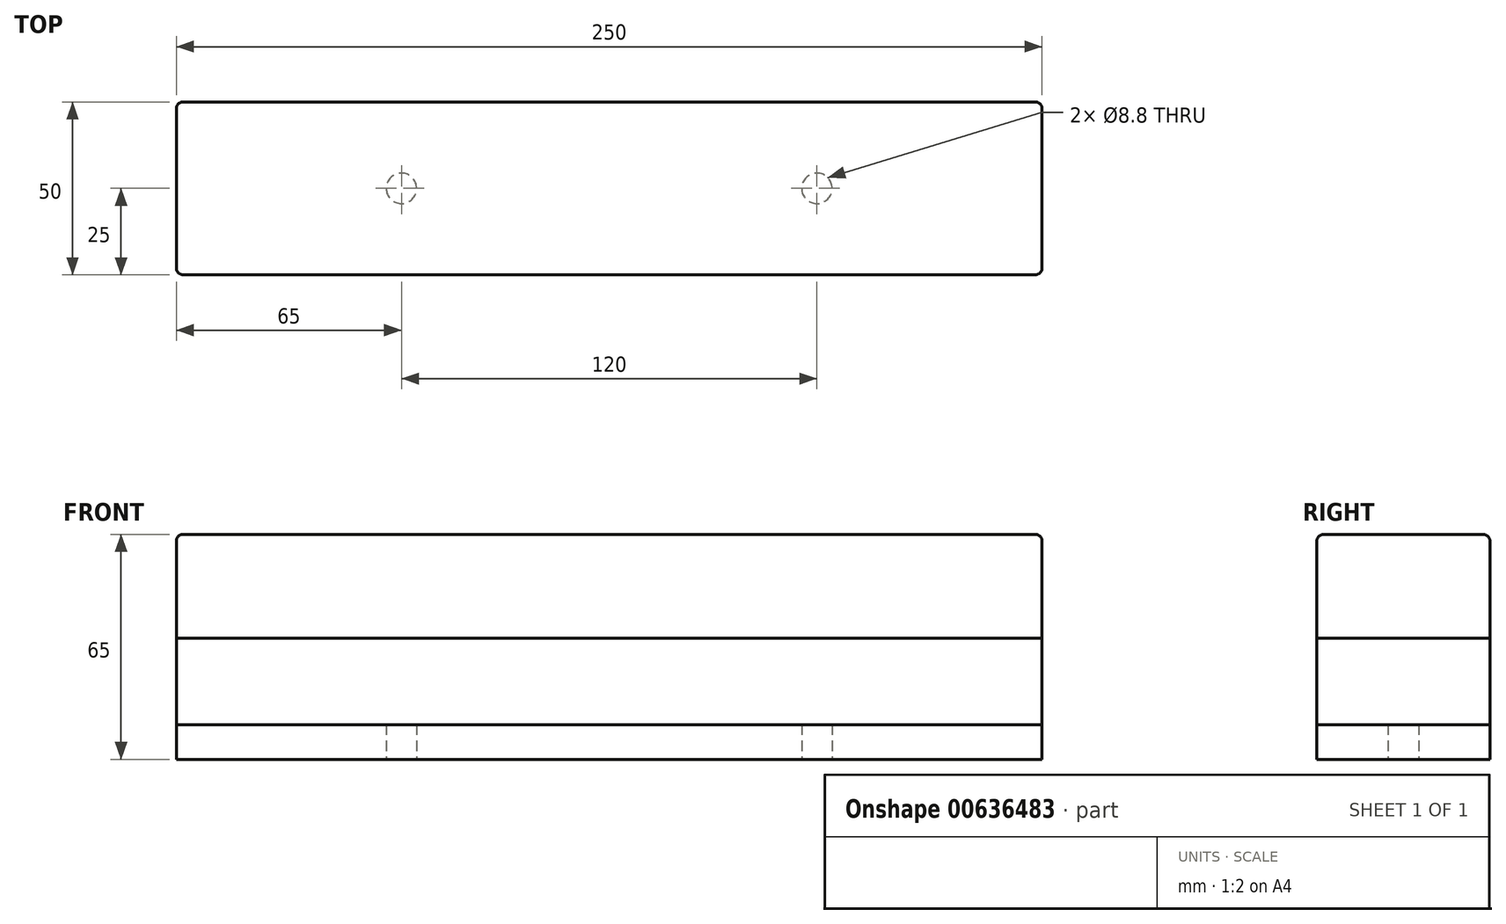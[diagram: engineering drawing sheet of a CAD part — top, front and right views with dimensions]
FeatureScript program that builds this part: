
annotation { "Feature Type Name" : "Feature", "Feature Type Description" : "" }
export const myFeature = defineFeature(function(context is Context, id is Id, definition is map)
    precondition{}
    {
        {
            var Q0;
            Q0=qCreatedBy(makeId("Top.planeOp"),FACE);
            var sketch = newSketch(context, id + "F0", { "sketchPlane" : qUnion([Q0])});
            skLineSegment(sketch, "E0.bottom", {"start": v(125, -25) * mm, "end": v(-125, -25) * mm});
            skLineSegment(sketch, "E0.top", {"start": v(125, 25) * mm, "end": v(-125, 25) * mm});
            skLineSegment(sketch, "E0.left", {"start": v(125, -25) * mm, "end": v(125, 25) * mm});
            skLineSegment(sketch, "E0.right", {"start": v(-125, -25) * mm, "end": v(-125, 25) * mm});
            skPoint(sketch, "E0.middle", {"position": v(0, 0) * mm});
            skPoint(sketch, "E1", {"position": v(-60, 0) * mm});
            skPoint(sketch, "E2", {"position": v(60, 0) * mm});
            skSolve(sketch);
        }
        {
            var Q0;
            Q0 = qSketchRegion(id + "F0", true);
            extrude(context, id + "F1", {"entities" : qUnion([Q0]), "depth" : 10 * mm, "offsetDistance" : 25 * mm});
        }
        {
            var Q0;
            Q0=makeQuery(id+"F1.opExtrude","CAP_FACE",FACE,{"disambiguationData":[OSD([sQuery(id+"F0.wireOp",EDGE,"E0.bottom"),sQuery(id+"F0.wireOp",EDGE,"E0.top"),sQuery(id+"F0.wireOp",EDGE,"E0.left"),sQuery(id+"F0.wireOp",EDGE,"E0.right")])],"isStart":false});
            var sketch = newSketch(context, id + "F2", { "sketchPlane" : qUnion([Q0])});
            skLineSegment(sketch, "E3", {"start": v(-125, 25) * mm, "end": v(-125, -25) * mm});
            skLineSegment(sketch, "E4", {"start": v(-125, 25) * mm, "end": v(125, 25) * mm});
            skLineSegment(sketch, "E5", {"start": v(125, 25) * mm, "end": v(125, -25) * mm});
            skLineSegment(sketch, "E6", {"start": v(125, -25) * mm, "end": v(-119.99, -25) * mm});
            skLineSegment(sketch, "E7", {"start": v(-119.99, -25) * mm, "end": v(-125, -25) * mm});
            skSolve(sketch);
        }
        {
            var Q0;
            Q0=makeQuery(id+"F2.imprint","IMPRINT",FACE,{"disambiguationData":[TD([[makeQuery(id+"F2.imprint","IMPRINT",EDGE,{"derivedFrom":sQuery(id+"F2.wireOp",EDGE,"E3")}),-1.0]])]});
            extrude(context, id + "F3", {"entities" : qUnion([Q0]), "depth" : 25 * mm, "offsetDistance" : 25 * mm});
        }
        {
            var Q0;
            Q0=makeQuery(id+"F3.opExtrude","CAP_FACE",FACE,{"disambiguationData":[OSD([sQuery(id+"F2.wireOp",EDGE,"E3"),sQuery(id+"F2.wireOp",EDGE,"E4"),sQuery(id+"F2.wireOp",EDGE,"E5"),sQuery(id+"F2.wireOp",EDGE,"E6"),sQuery(id+"F2.wireOp",EDGE,"E7")])],"isStart":false});
            var sketch = newSketch(context, id + "F4", { "sketchPlane" : qUnion([Q0])});
            skLineSegment(sketch, "E8", {"start": v(-125, 25) * mm, "end": v(-125, -25) * mm});
            skLineSegment(sketch, "E9", {"start": v(-125, -25) * mm, "end": v(125, -25) * mm});
            skLineSegment(sketch, "E10", {"start": v(125, -25) * mm, "end": v(125, 25) * mm});
            skLineSegment(sketch, "E11", {"start": v(125, 25) * mm, "end": v(-125, 25) * mm});
            skSolve(sketch);
        }
        {
            var Q0;
            Q0=sQuery(id+"F0.wireOp",VERTEX,"E1");
            var Q1;
            Q1=sQuery(id+"F0.wireOp",VERTEX,"E2");
            var Q2;
            Q2=makeQuery(id+"F1.opExtrude","SWEPT_BODY",BODY,{"disambiguationData":[OSD([sQuery(id+"F0.wireOp",EDGE,"E0.bottom"),sQuery(id+"F0.wireOp",EDGE,"E0.top"),sQuery(id+"F0.wireOp",EDGE,"E0.left"),sQuery(id+"F0.wireOp",EDGE,"E0.right")])]});
            hole(context, id + "F5", {"style" : HoleStyle.SIMPLE, "endStyle" : HoleEndStyle.BLIND, "oppositeDirection" : true, "standardTappedOrClearance" : lookupTablePath({ "standard" : "ISO", "fit" : "Normal", "size" : "M8", "type" : "Clearance" }), "standardBlindInLast" : lookupTablePath({ "fit" : "Standard", "standard" : "ISO", "size" : "M8", "type" : "Clearance" }), "holeDiameter" : 8.8 * mm, "majorDiameter" : 5 * mm, "holeDepth" : 10 * mm, "isTappedThrough" : true, "tappedDepth" : 8 * mm, "tapClearance" : 3, "startFromSketch" : true, "locations" : qUnion([Q0, Q1]), "scope" : qUnion([Q2])});
        }
        {
            var Q0;
            Q0=makeQuery(id+"F4.imprint","IMPRINT",FACE,{"disambiguationData":[TD([[makeQuery(id+"F4.imprint","IMPRINT",EDGE,{"derivedFrom":sQuery(id+"F4.wireOp",EDGE,"E8")}),-1.0]])]});
            extrude(context, id + "F6", {"entities" : qUnion([Q0]), "depth" : 30 * mm, "offsetDistance" : 25 * mm});
        }
        {
            var Q0;
            Q0=makeQuery(id+"F1.opExtrude","SWEPT_EDGE",EDGE,{"disambiguationData":[OSD([sQuery(id+"F0.wireOp",EDGE,"E0.bottom"),sQuery(id+"F0.wireOp",EDGE,"E0.right")])]});
            var Q1;
            Q1=makeQuery(id+"F1.opExtrude","SWEPT_EDGE",EDGE,{"disambiguationData":[OSD([sQuery(id+"F0.wireOp",EDGE,"E0.top"),sQuery(id+"F0.wireOp",EDGE,"E0.right")])]});
            var Q2;
            Q2=makeQuery(id+"F1.opExtrude","SWEPT_EDGE",EDGE,{"disambiguationData":[OSD([sQuery(id+"F0.wireOp",EDGE,"E0.top"),sQuery(id+"F0.wireOp",EDGE,"E0.left")])]});
            var Q3;
            Q3=makeQuery(id+"F1.opExtrude","SWEPT_EDGE",EDGE,{"disambiguationData":[OSD([sQuery(id+"F0.wireOp",EDGE,"E0.bottom"),sQuery(id+"F0.wireOp",EDGE,"E0.left")])]});
            var Q4;
            Q4=makeQuery(id+"F3.opExtrude","SWEPT_EDGE",EDGE,{"disambiguationData":[OSD([sQuery(id+"F2.wireOp",EDGE,"E3"),sQuery(id+"F2.wireOp",EDGE,"E7")])]});
            var Q5;
            Q5=makeQuery(id+"F3.opExtrude","SWEPT_EDGE",EDGE,{"disambiguationData":[OSD([sQuery(id+"F2.wireOp",EDGE,"E3"),sQuery(id+"F2.wireOp",EDGE,"E4")])]});
            var Q6;
            Q6=makeQuery(id+"F6.opExtrude","SWEPT_EDGE",EDGE,{"disambiguationData":[OSD([sQuery(id+"F4.wireOp",EDGE,"E8"),sQuery(id+"F4.wireOp",EDGE,"E9")])]});
            var Q7;
            Q7=makeQuery(id+"F6.opExtrude","SWEPT_EDGE",EDGE,{"disambiguationData":[OSD([sQuery(id+"F4.wireOp",EDGE,"E8"),sQuery(id+"F4.wireOp",EDGE,"E11")])]});
            var Q8;
            Q8=makeQuery(id+"F3.opExtrude","SWEPT_EDGE",EDGE,{"disambiguationData":[OSD([sQuery(id+"F2.wireOp",EDGE,"E5"),sQuery(id+"F2.wireOp",EDGE,"E6")])]});
            var Q9;
            Q9=makeQuery(id+"F6.opExtrude","SWEPT_EDGE",EDGE,{"disambiguationData":[OSD([sQuery(id+"F4.wireOp",EDGE,"E9"),sQuery(id+"F4.wireOp",EDGE,"E10")])]});
            var Q10;
            Q10=makeQuery(id+"F3.opExtrude","SWEPT_EDGE",EDGE,{"disambiguationData":[OSD([sQuery(id+"F2.wireOp",EDGE,"E4"),sQuery(id+"F2.wireOp",EDGE,"E5")])]});
            var Q11;
            Q11=makeQuery(id+"F6.opExtrude","SWEPT_EDGE",EDGE,{"disambiguationData":[OSD([sQuery(id+"F4.wireOp",EDGE,"E10"),sQuery(id+"F4.wireOp",EDGE,"E11")])]});
            var Q12;
            Q12=makeQuery(id+"F6.opExtrude","CAP_EDGE",EDGE,{"disambiguationData":[OSD([sQuery(id+"F4.wireOp",EDGE,"E11")])],"isStart":false});
            var Q13;
            Q13=makeQuery(id+"F6.opExtrude","CAP_EDGE",EDGE,{"disambiguationData":[OSD([sQuery(id+"F4.wireOp",EDGE,"E10")])],"isStart":false});
            var Q14;
            Q14=makeQuery(id+"F6.opExtrude","CAP_EDGE",EDGE,{"disambiguationData":[OSD([sQuery(id+"F4.wireOp",EDGE,"E9")])],"isStart":false});
            var Q15;
            Q15=makeQuery(id+"F6.opExtrude","CAP_EDGE",EDGE,{"disambiguationData":[OSD([sQuery(id+"F4.wireOp",EDGE,"E8")])],"isStart":false});
            fillet(context, id + "F7", {"entities" : qUnion([Q0, Q1, Q2, Q3, Q4, Q5, Q6, Q7, Q8, Q9, Q10, Q11, Q12, Q13, Q14, Q15]), "radius" : 2 * mm, "tangentPropagation" : true, "allowEdgeOverflow" : false});
        }
    });
